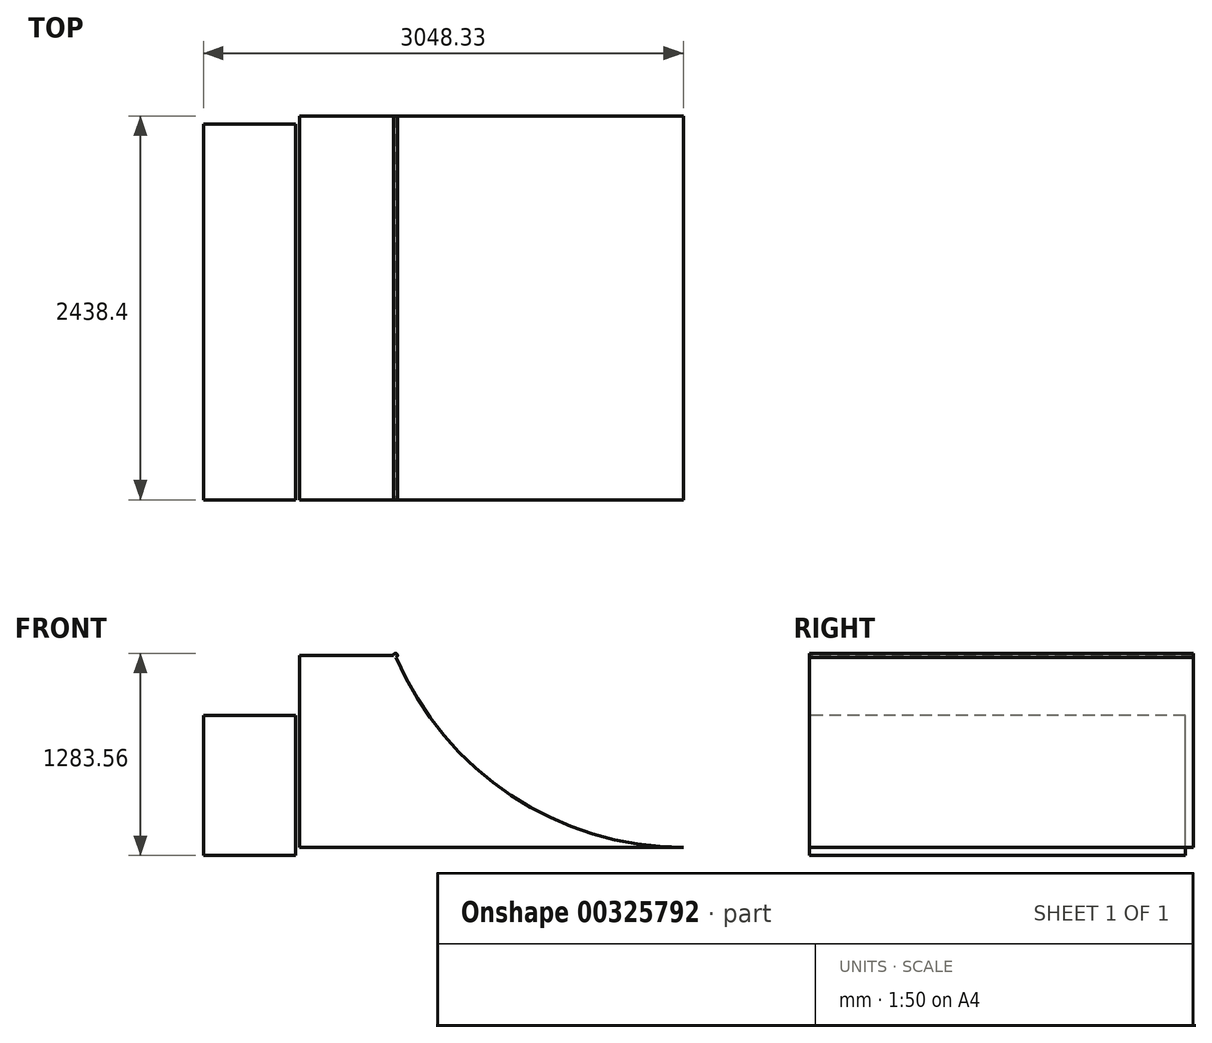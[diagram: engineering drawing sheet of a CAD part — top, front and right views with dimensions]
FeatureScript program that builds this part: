
annotation { "Feature Type Name" : "Feature", "Feature Type Description" : "" }
export const myFeature = defineFeature(function(context is Context, id is Id, definition is map)
    precondition{}
    {
        {
            var Q0;
            Q0=qCreatedBy(makeId("Front.planeOp"),FACE);
            var sketch = newSketch(context, id + "F0", { "sketchPlane" : qUnion([Q0])});
            skLineSegment(sketch, "E0.bottom", {"start": v(0, 0) * mm, "end": v(-2438.4, 0) * mm});
            skLineSegment(sketch, "E0.top", {"start": v(0, 1219.2) * mm, "end": v(-2438.4, 1219.2) * mm});
            skLineSegment(sketch, "E0.left", {"start": v(0, 0) * mm, "end": v(0, 1219.2) * mm});
            skLineSegment(sketch, "E0.right", {"start": v(-2438.4, 0) * mm, "end": v(-2438.4, 1219.2) * mm});
            skArc(sketch, "E1", {"start": v(-1828.8, 1219.2) * mm, "mid": v(-1098.97, 332.74) * mm, "end": v(0, 0) * mm});
            skCircle(sketch, "E2", {"center": v(-1828.8, 1219.2) * mm, "radius": 12.7 * mm});
            skSolve(sketch);
        }
        {
            var Q0;
            {var subQ1=sQuery(id+"F0.wireOp",EDGE,"E0.bottom");Q0=makeQuery(id+"F0.imprint","IMPRINT",FACE,{"disambiguationData":[TD([[makeQuery(id+"F0.imprint","IMPRINT",EDGE,{"derivedFrom":subQ1}),-1.0]])]});}
            var Q1;
            {var subQ0=sQuery(id+"F0.wireOp",EDGE,"E0.top");var subQ1=makeQuery(id+"F0.imprint","INTERSECT",VERTEX,{"derivedFrom":[subQ0,sQuery(id+"F0.wireOp",EDGE,"E1")]});Q1=makeQuery(id+"F0.imprint","IMPRINT",FACE,{"disambiguationData":[TD([[makeQuery(id+"F0.imprint","IMPRINT",EDGE,{"disambiguationData":[TD([[subQ1,1.0]])],"derivedFrom":subQ0}),-1.0]])]});}
            var Q2;
            {var subQ0=sQuery(id+"F0.wireOp",EDGE,"E1");var subQ1=sQuery(id+"F0.wireOp",EDGE,"E0.top");var subQ2=makeQuery(id+"F0.imprint","INTERSECT",VERTEX,{"derivedFrom":[subQ1,subQ0]});Q2=makeQuery(id+"F0.imprint","IMPRINT",FACE,{"disambiguationData":[TD([[makeQuery(id+"F0.imprint","IMPRINT",EDGE,{"disambiguationData":[TD([[subQ2,1.0]])],"derivedFrom":subQ1}),1.0]])]});}
            var Q3;
            {var subQ0=sQuery(id+"F0.wireOp",EDGE,"E1");var subQ1=sQuery(id+"F0.wireOp",EDGE,"E0.top");var subQ2=makeQuery(id+"F0.imprint","INTERSECT",VERTEX,{"derivedFrom":[subQ1,subQ0]});Q3=makeQuery(id+"F0.imprint","IMPRINT",FACE,{"disambiguationData":[TD([[makeQuery(id+"F0.imprint","IMPRINT",EDGE,{"disambiguationData":[TD([[subQ2,-1.0]])],"derivedFrom":subQ1}),1.0]])]});}
            extrude(context, id + "F1", {"entities" : qUnion([Q0, Q1, Q2, Q3]), "endBound" : BoundingType.SYMMETRIC, "oppositeDirection" : true, "depth" : 2438.4 * mm});
        }
        {
            var Q0;
            Q0=makeQuery(id+"F1.opExtrude","SWEPT_FACE",FACE,{"disambiguationData":[OSD([sQuery(id+"F0.wireOp",EDGE,"E0.top")])]});
            var sketch = newSketch(context, id + "F2", { "sketchPlane" : qUnion([Q0])});
            skLineSegment(sketch, "E3.bottom", {"start": v(-2894.3, 1168.17) * mm, "end": v(-3480.13, 1168.17) * mm});
            skLineSegment(sketch, "E3.top", {"start": v(-2894.3, -1219.2) * mm, "end": v(-3480.13, -1219.2) * mm});
            skLineSegment(sketch, "E3.left", {"start": v(-2894.3, 1168.17) * mm, "end": v(-2894.3, -1219.2) * mm});
            skLineSegment(sketch, "E3.right", {"start": v(-3480.13, 1168.17) * mm, "end": v(-3480.13, -1219.2) * mm});
            skSolve(sketch);
        }
        {
            var Q0;
            Q0=makeQuery(id+"F2.imprint","IMPRINT",FACE,{"disambiguationData":[TD([[makeQuery(id+"F2.imprint","IMPRINT",EDGE,{"derivedFrom":sQuery(id+"F2.wireOp",EDGE,"E3.bottom")}),1.0]])]});
            extrude(context, id + "F3", {"entities" : qUnion([Q0]), "oppositeDirection" : true, "depth" : 889.86 * mm});
        }
        {
            var Q0;
            Q0=makeQuery(id+"F3.opExtrude","SWEPT_BODY",BODY,{"disambiguationData":[OSD([sQuery(id+"F2.wireOp",EDGE,"E3.bottom"),sQuery(id+"F2.wireOp",EDGE,"E3.top"),sQuery(id+"F2.wireOp",EDGE,"E3.left"),sQuery(id+"F2.wireOp",EDGE,"E3.right")])]});
            transform(context, id + "F4", {"entities" : qUnion([Q0]), "transformType" : TransformType.TRANSLATION_3D, "dx" : 431.8 * mm, "dy" : 0 * mm, "dz" : -381 * mm, "makeCopy" : false});
        }
    });
